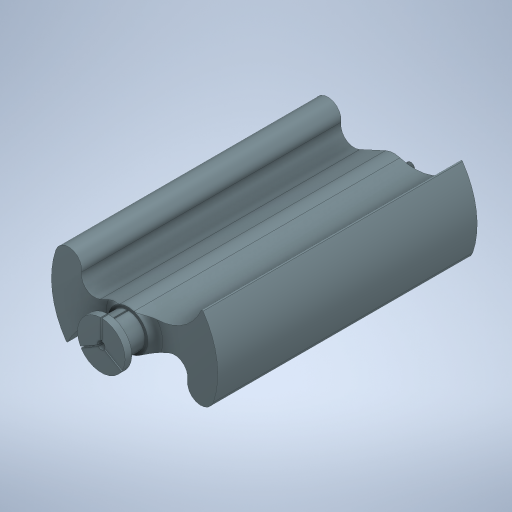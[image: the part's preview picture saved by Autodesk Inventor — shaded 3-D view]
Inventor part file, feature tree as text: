
AUTODESK INVENTOR PART (.ipt)
format: ipt  version: 2024 (Build 280153000, 153)  size: 641,024 bytes
history: native  units: in
note: dims shown in document units (in); Inventor stores cm internally (conversion verified against a paired STEP export)
features: extrude x7, sketch x7, projected_geometry x4, plane x2, revolve x1, pattern_circular x1, fillet x1
ambient origin geometry x8: Origin, YZ Plane, XZ Plane, XY Plane, X Axis, Y Axis, Z Axis, Center Point
bodies: Solid1 (feature_tree)
feature tree (23):
  extrude  "Extrusion1"  Depth=0.025in TaperAngle=0.0deg
  sketch  "Sketch2"  dims[d13=0.25in d14=0.0in d15=0.2in]
  extrude  "Extrusion2"  Depth=0.2in
  extrude  "Extrusion3"  Depth=0.6in
  revolve  "Revolution1"  [1 undecoded]
  extrude  "Extrusion7"  Depth=0.155in TaperAngle=0.0deg
  pattern_circular  "Circular Pattern1"  [2 undecoded]
  fillet  "Fillet1"  Radius=0.2in
  extrude  "Extrusion4"  Depth=0.125in
  plane  "Work Plane1"
  extrude  "Extrusion5"  Depth=0.125in
  plane  "Work Plane2"
  extrude  "Extrusion6"  Depth=0.125in
  sketch  "Sketch1"  dims[d0=2.5in d1=0.5in d3=3.9in d4=0.0in d11=0.025in d12=0.0in]
  sketch  "Sketch3"  dims[d16=1.0in d17=0.0in d24=0.6in]
  sketch  "Sketch4"  dims[d27=0.375in d51=-0.25in]
  projected_geometry  "Projected Loop1"
  sketch  "Sketch5"  dims[d52=0.32in d53=0.155in d54=0.0in]
  projected_geometry  "Projected Loop2"
  sketch  "Sketch7"  dims[d55=0.0in]
  projected_geometry  "Projected Loop4"
  sketch  "Sketch8"  dims[d56=0.0039in d57=0.0in d62=2.5in d64=0.2in d65=0.2in d71=0.0312in d72=0.7in d73=0.75in d74=0.4in d75=0.7874in d77=360.0deg d79=0.1in d80=0.1in d81=0.3in d82=0.4in d83=0.0575in d84=90.0deg d85=0.01in d86=0.02in d87=1.0in d88=0.0in d89=1.1811in d90=360.0deg d92=0.125in]
  projected_geometry  "Projected Loop5"
note: 3 required parameter values undecoded (feature->parameter linkage not recoverable at this tier; creation-order binding heuristic only, values carry confidence <= 0.55)